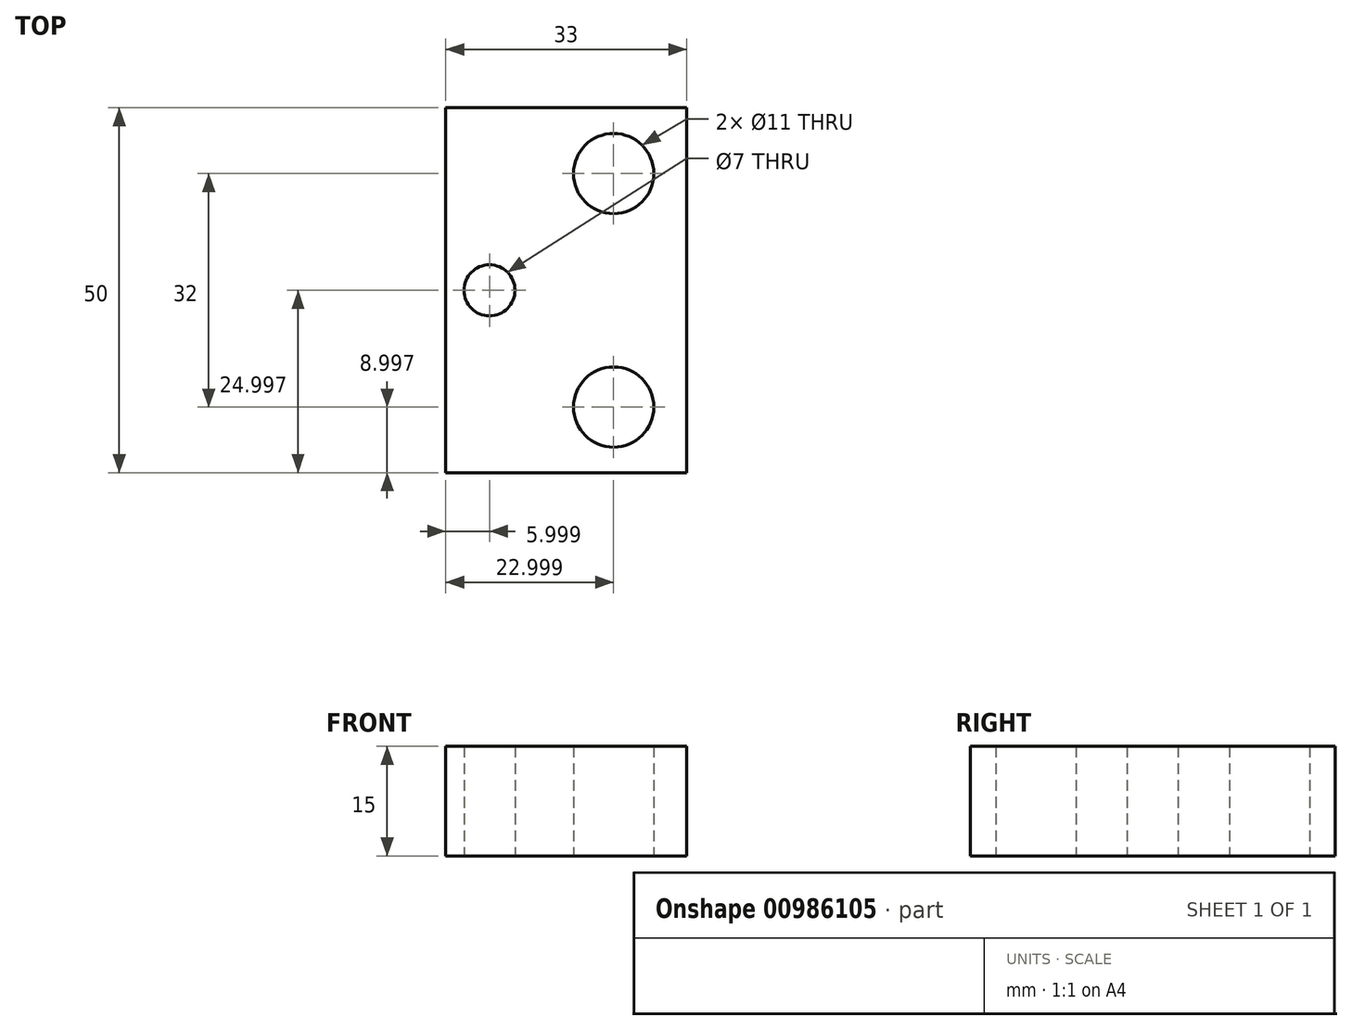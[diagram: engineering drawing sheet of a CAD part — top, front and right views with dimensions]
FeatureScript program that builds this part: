
annotation { "Feature Type Name" : "Feature", "Feature Type Description" : "" }
export const myFeature = defineFeature(function(context is Context, id is Id, definition is map)
    precondition{}
    {
        {
            var Q0;
            Q0=qCreatedBy(makeId("Top.planeOp"),FACE);
            var sketch = newSketch(context, id + "F0", { "sketchPlane" : qUnion([Q0])});
            skLineSegment(sketch, "E0.bottom", {"start": v(-0.01, 0) * mm, "end": v(32.99, 0) * mm});
            skLineSegment(sketch, "E0.top", {"start": v(-0.01, 50) * mm, "end": v(32.99, 50) * mm});
            skLineSegment(sketch, "E0.left", {"start": v(-0.01, 0) * mm, "end": v(-0.01, 50) * mm});
            skLineSegment(sketch, "E0.right", {"start": v(32.99, 0) * mm, "end": v(32.99, 50) * mm});
            skLineSegment(sketch, "E1", {"start": v(-0.01, 25) * mm, "end": v(36.63, 25) * mm, "construction": true});
            skCircle(sketch, "E2", {"center": v(22.99, 41) * mm, "radius": 3.5 * mm});
            skCircle(sketch, "E3", {"center": v(22.99, 41) * mm, "radius": 5.5 * mm});
            skCircle(sketch, "E4", {"center": v(22.99, 9) * mm, "radius": 3.5 * mm});
            skCircle(sketch, "E5", {"center": v(22.99, 9) * mm, "radius": 5.5 * mm});
            skCircle(sketch, "E6", {"center": v(5.99, 25) * mm, "radius": 3.5 * mm});
            skLineSegment(sketch, "E7.0", {"start": v(12.99, 0) * mm, "end": v(12.99, 50) * mm, "construction": true});
            skSolve(sketch);
        }
        {
            var Q0;
            Q0 = qSketchRegion(id + "F0", true);
            extrude(context, id + "F1", {"entities" : qUnion([Q0]), "depth" : 15 * mm, "offsetDistance" : 25 * mm});
        }
    });
